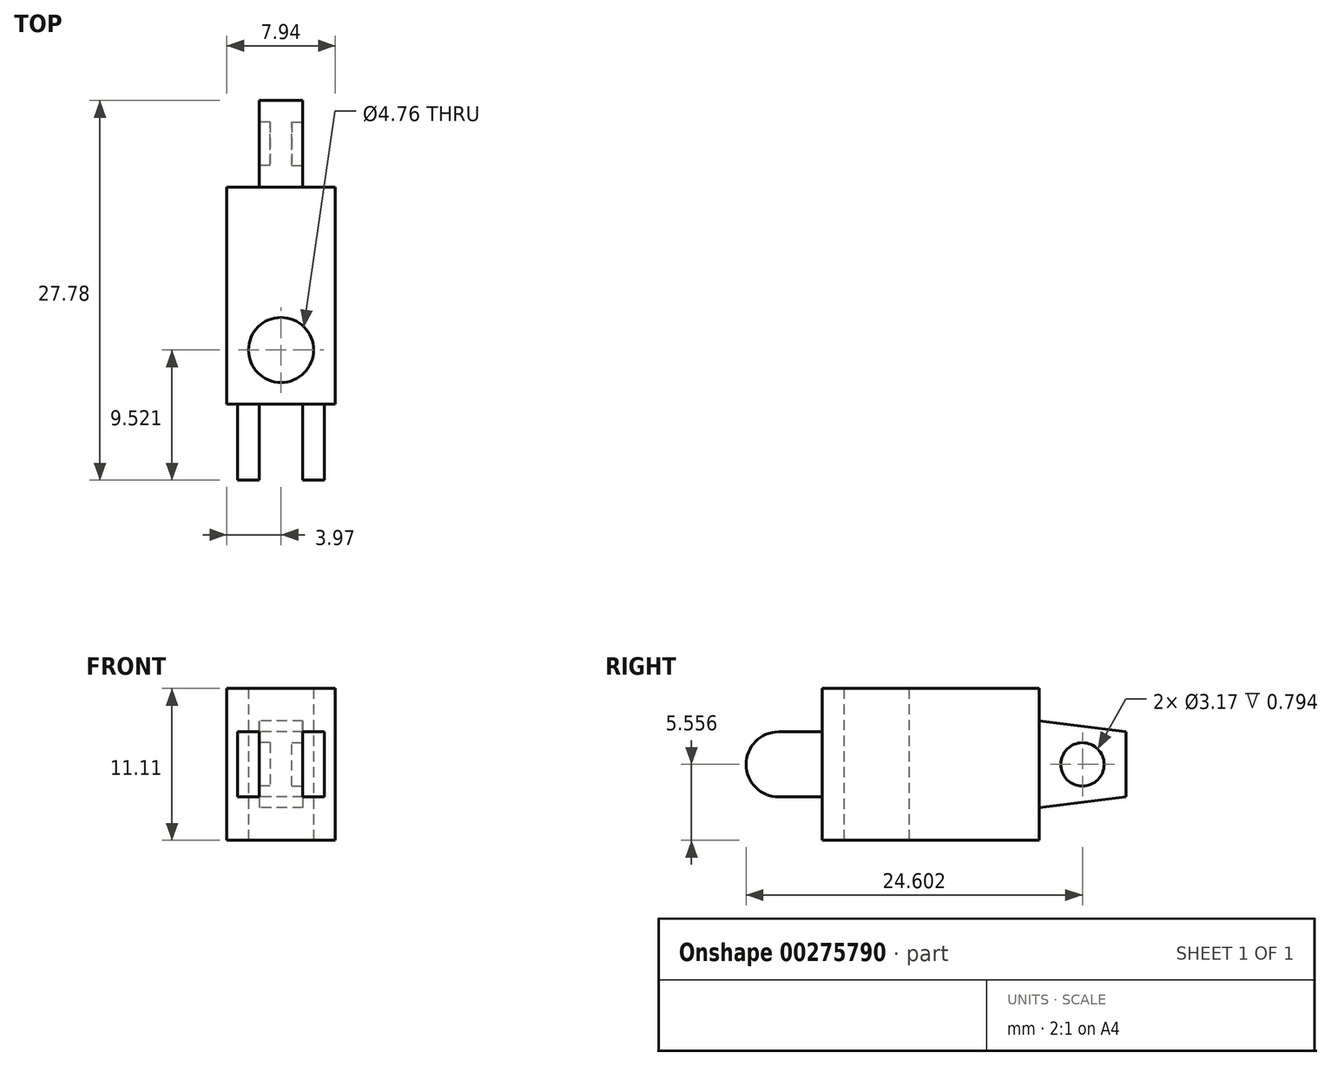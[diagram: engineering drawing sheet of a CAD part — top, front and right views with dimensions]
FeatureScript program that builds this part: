
annotation { "Feature Type Name" : "Feature", "Feature Type Description" : "" }
export const myFeature = defineFeature(function(context is Context, id is Id, definition is map)
    precondition{}
    {
        {
            var Q0;
            Q0=qCreatedBy(makeId("Top.planeOp"),FACE);
            var sketch = newSketch(context, id + "F0", { "sketchPlane" : qUnion([Q0])});
            skLineSegment(sketch, "E0.bottom", {"start": v(-3.97, 7.94) * mm, "end": v(3.97, 7.94) * mm});
            skLineSegment(sketch, "E0.top", {"start": v(-3.97, -7.94) * mm, "end": v(3.97, -7.94) * mm});
            skLineSegment(sketch, "E0.left", {"start": v(-3.97, 7.94) * mm, "end": v(-3.97, -7.94) * mm});
            skLineSegment(sketch, "E0.right", {"start": v(3.97, 7.94) * mm, "end": v(3.97, -7.94) * mm});
            skPoint(sketch, "E0.middle", {"position": v(0, 0) * mm});
            skCircle(sketch, "E1", {"center": v(0, 3.97) * mm, "radius": 2.38 * mm});
            skCircle(sketch, "E2.MirrorC", {"center": v(0, -3.97) * mm, "radius": 2.38 * mm});
            skSolve(sketch);
        }
        {
            var Q0;
            Q0=qSketchRegion(id+"F0",true);
            extrude(context, id + "F1", {"entities" : qUnion([Q0]), "depth" : 9.52 * mm});
        }
        {
            var Q0;
            Q0=makeQuery(id+"F0.imprint","IMPRINT",FACE,{"disambiguationData":[TD([[makeQuery(id+"F0.imprint","IMPRINT",EDGE,{"derivedFrom":sQuery(id+"F0.wireOp",EDGE,"E1")}),1.0]])]});
            var Q1;
            Q1=makeQuery(id+"F0.imprint","IMPRINT",FACE,{"disambiguationData":[TD([[makeQuery(id+"F0.imprint","IMPRINT",EDGE,{"derivedFrom":sQuery(id+"F0.wireOp",EDGE,"E2.MirrorC")}),-1.0]])]});
            extrude(context, id + "F2", {"entities" : qUnion([Q0, Q1]), "operationType" : NewBodyOperationType.ADD, "depth" : 11.1 * mm});
        }
        {
            var Q0;
            Q0=qCreatedBy(makeId("Right.planeOp"),FACE);
            var sketch = newSketch(context, id + "F3", { "sketchPlane" : qUnion([Q0])});
            skLineSegment(sketch, "E3", {"start": v(0, 5.56) * mm, "end": v(-7.94, 5.56) * mm});
            skLineSegment(sketch, "E4", {"start": v(-7.94, 5.56) * mm, "end": v(-7.94, 7.94) * mm});
            skLineSegment(sketch, "E5.bottom", {"start": v(-7.94, 7.94) * mm, "end": v(-11.11, 7.94) * mm});
            skLineSegment(sketch, "E5.top", {"start": v(-7.94, 5.56) * mm, "end": v(-11.11, 5.56) * mm});
            skLineSegment(sketch, "E5.left", {"start": v(-7.94, 7.94) * mm, "end": v(-7.94, 5.56) * mm});
            skLineSegment(sketch, "E5.right", {"start": v(-11.11, 7.94) * mm, "end": v(-11.11, 5.56) * mm});
            skLineSegment(sketch, "E6.MirrorCS", {"start": v(-11.11, 3.17) * mm, "end": v(-11.11, 5.56) * mm});
            skLineSegment(sketch, "E7.MirrorCS", {"start": v(-7.94, 3.17) * mm, "end": v(-11.11, 3.17) * mm});
            skLineSegment(sketch, "E8.MirrorCS", {"start": v(-7.94, 3.17) * mm, "end": v(-7.94, 5.56) * mm});
            skLineSegment(sketch, "E9", {"start": v(-11.11, 5.56) * mm, "end": v(-13.5, 5.56) * mm});
            skArc(sketch, "E10", {"start": v(-11.11, 7.94) * mm, "mid": v(-13.5, 5.56) * mm, "end": v(-11.11, 3.17) * mm});
            skLineSegment(sketch, "E11", {"start": v(0, 5.56) * mm, "end": v(7.94, 5.56) * mm});
            skLineSegment(sketch, "E12", {"start": v(7.94, 5.56) * mm, "end": v(14.29, 5.56) * mm});
            skLineSegment(sketch, "E13", {"start": v(14.29, 5.56) * mm, "end": v(14.29, 7.94) * mm});
            skLineSegment(sketch, "E14", {"start": v(14.29, 7.94) * mm, "end": v(7.94, 8.73) * mm});
            skLineSegment(sketch, "E15", {"start": v(7.94, 8.73) * mm, "end": v(7.94, 5.56) * mm});
            skLineSegment(sketch, "E16.MirrorCS", {"start": v(14.29, 5.56) * mm, "end": v(14.29, 3.18) * mm});
            skLineSegment(sketch, "E17.MirrorCS", {"start": v(14.29, 3.18) * mm, "end": v(7.94, 2.38) * mm});
            skLineSegment(sketch, "E18.MirrorCS", {"start": v(7.94, 2.38) * mm, "end": v(7.94, 5.56) * mm});
            skSolve(sketch);
        }
        {
            var Q0;
            Q0=makeQuery(id+"F3.imprint","IMPRINT",FACE,{"disambiguationData":[TD([[makeQuery(id+"F3.imprint","IMPRINT",EDGE,{"derivedFrom":sQuery(id+"F3.wireOp",EDGE,"E5.bottom")}),1.0]])]});
            var Q1;
            Q1=makeQuery(id+"F3.imprint","IMPRINT",FACE,{"disambiguationData":[TD([[makeQuery(id+"F3.imprint","IMPRINT",EDGE,{"derivedFrom":sQuery(id+"F3.wireOp",EDGE,"E5.top")}),1.0]])]});
            var Q2;
            {var subQ0=sQuery(id+"F3.wireOp",EDGE,"E5.right");Q2=makeQuery(id+"F3.imprint","IMPRINT",FACE,{"disambiguationData":[TD([[makeQuery(id+"F3.imprint","IMPRINT",EDGE,{"derivedFrom":subQ0}),-1.0]])]});}
            var Q3;
            {var subQ0=sQuery(id+"F3.wireOp",EDGE,"E6.MirrorCS");Q3=makeQuery(id+"F3.imprint","IMPRINT",FACE,{"disambiguationData":[TD([[makeQuery(id+"F3.imprint","IMPRINT",EDGE,{"derivedFrom":subQ0}),1.0]])]});}
            extrude(context, id + "F4", {"entities" : qUnion([Q0, Q1, Q2, Q3]), "operationType" : NewBodyOperationType.ADD, "endBound" : BoundingType.SYMMETRIC, "depth" : 6.35 * mm});
        }
        {
            var Q0;
            Q0=makeQuery(id+"F4.opExtrude","SWEPT_FACE",FACE,{"disambiguationData":[OSD([sQuery(id+"F3.wireOp",EDGE,"E5.bottom")])]});
            var sketch = newSketch(context, id + "F5", { "sketchPlane" : qUnion([Q0])});
            skLineSegment(sketch, "E19", {"start": v(0, -7.94) * mm, "end": v(0, -14.29) * mm});
            skPoint(sketch, "E19.endSnap0", {"position": v(0, -11.11) * mm});
            skLineSegment(sketch, "E20", {"start": v(0, -14.29) * mm, "end": v(-1.59, -14.29) * mm});
            skLineSegment(sketch, "E21", {"start": v(-1.59, -14.29) * mm, "end": v(-1.59, -7.94) * mm});
            skLineSegment(sketch, "E22", {"start": v(-1.59, -7.94) * mm, "end": v(0, -7.94) * mm});
            skLineSegment(sketch, "E23.MirrorCS", {"start": v(1.59, -7.94) * mm, "end": v(0, -7.94) * mm});
            skLineSegment(sketch, "E24.MirrorCS", {"start": v(1.59, -14.29) * mm, "end": v(1.59, -7.94) * mm});
            skLineSegment(sketch, "E25.MirrorCS", {"start": v(0, -14.29) * mm, "end": v(1.59, -14.29) * mm});
            skSolve(sketch);
        }
        {
            var Q0;
            Q0=qSketchRegion(id+"F5",true);
            extrude(context, id + "F6", {"entities" : qUnion([Q0]), "operationType" : NewBodyOperationType.REMOVE, "oppositeDirection" : true, "depth" : 6.35 * mm});
        }
        {
            var Q0;
            Q0=makeQuery(id+"F3.imprint","IMPRINT",FACE,{"disambiguationData":[TD([[makeQuery(id+"F3.imprint","IMPRINT",EDGE,{"derivedFrom":sQuery(id+"F3.wireOp",EDGE,"E12")}),1.0]])]});
            var Q1;
            Q1=makeQuery(id+"F3.imprint","IMPRINT",FACE,{"disambiguationData":[TD([[makeQuery(id+"F3.imprint","IMPRINT",EDGE,{"derivedFrom":sQuery(id+"F3.wireOp",EDGE,"E12")}),-1.0]])]});
            extrude(context, id + "F7", {"entities" : qUnion([Q0, Q1]), "operationType" : NewBodyOperationType.ADD, "endBound" : BoundingType.SYMMETRIC, "depth" : 3.17 * mm});
        }
        {
            var Q0;
            Q0=makeQuery(id+"F7.opExtrude","CAP_FACE",FACE,{"disambiguationData":[OSD([sQuery(id+"F3.wireOp",EDGE,"E13"),sQuery(id+"F3.wireOp",EDGE,"E14"),sQuery(id+"F3.wireOp",EDGE,"E15"),sQuery(id+"F3.wireOp",EDGE,"E16.MirrorCS"),sQuery(id+"F3.wireOp",EDGE,"E17.MirrorCS"),sQuery(id+"F3.wireOp",EDGE,"E18.MirrorCS")])],"isStart":false});
            var sketch = newSketch(context, id + "F8", { "sketchPlane" : qUnion([Q0])});
            skCircle(sketch, "E26", {"center": v(11.11, 5.56) * mm, "radius": 1.59 * mm});
            skPoint(sketch, "E26.centerSnap0", {"position": v(14.29, 5.56) * mm});
            skSolve(sketch);
        }
        {
            var Q0;
            Q0=qSketchRegion(id+"F8",true);
            extrude(context, id + "F9", {"entities" : qUnion([Q0]), "operationType" : NewBodyOperationType.REMOVE, "oppositeDirection" : true, "depth" : 0.8 * mm});
        }
        {
            var Q0;
            Q0=makeQuery(id+"F7.opExtrude","CAP_FACE",FACE,{"disambiguationData":[OSD([sQuery(id+"F3.wireOp",EDGE,"E13"),sQuery(id+"F3.wireOp",EDGE,"E14"),sQuery(id+"F3.wireOp",EDGE,"E15"),sQuery(id+"F3.wireOp",EDGE,"E16.MirrorCS"),sQuery(id+"F3.wireOp",EDGE,"E17.MirrorCS"),sQuery(id+"F3.wireOp",EDGE,"E18.MirrorCS")])],"isStart":true});
            var sketch = newSketch(context, id + "F10", { "sketchPlane" : qUnion([Q0])});
            skCircle(sketch, "E27", {"center": v(-11.11, 5.56) * mm, "radius": 1.59 * mm});
            skSolve(sketch);
        }
        {
            var Q0;
            Q0=qSketchRegion(id+"F10",true);
            extrude(context, id + "F11", {"entities" : qUnion([Q0]), "operationType" : NewBodyOperationType.REMOVE, "oppositeDirection" : true, "depth" : 0.8 * mm});
        }
    });
